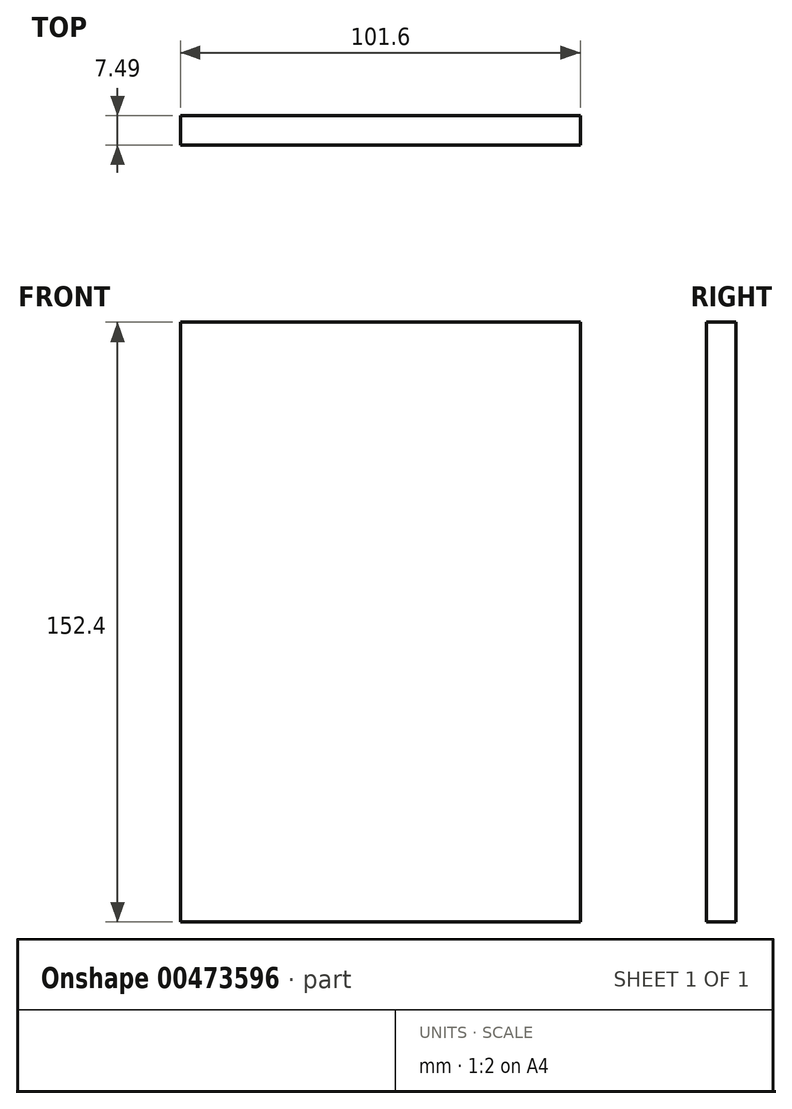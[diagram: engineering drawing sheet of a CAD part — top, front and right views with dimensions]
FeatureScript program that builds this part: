
annotation { "Feature Type Name" : "Feature", "Feature Type Description" : "" }
export const myFeature = defineFeature(function(context is Context, id is Id, definition is map)
    precondition{}
    {
        {
            var Q0;
            Q0=qCreatedBy(makeId("Front.planeOp"),FACE);
            var sketch = newSketch(context, id + "F0", { "sketchPlane" : qUnion([Q0])});
            skLineSegment(sketch, "E0", {"start": v(-49.16, -25.36) * mm, "end": v(52.44, -25.36) * mm});
            skLineSegment(sketch, "E1", {"start": v(-49.16, -25.36) * mm, "end": v(-49.16, 127.04) * mm});
            skLineSegment(sketch, "E2", {"start": v(-49.16, 127.04) * mm, "end": v(52.44, 127.04) * mm});
            skLineSegment(sketch, "E3", {"start": v(52.44, 127.04) * mm, "end": v(52.44, -25.36) * mm});
            skSolve(sketch);
        }
        {
            var Q0;
            Q0 = qSketchRegion(id + "F0", true);
            extrude(context, id + "F1", {"entities" : qUnion([Q0]), "depth" : 7.5 * mm});
        }
    });
